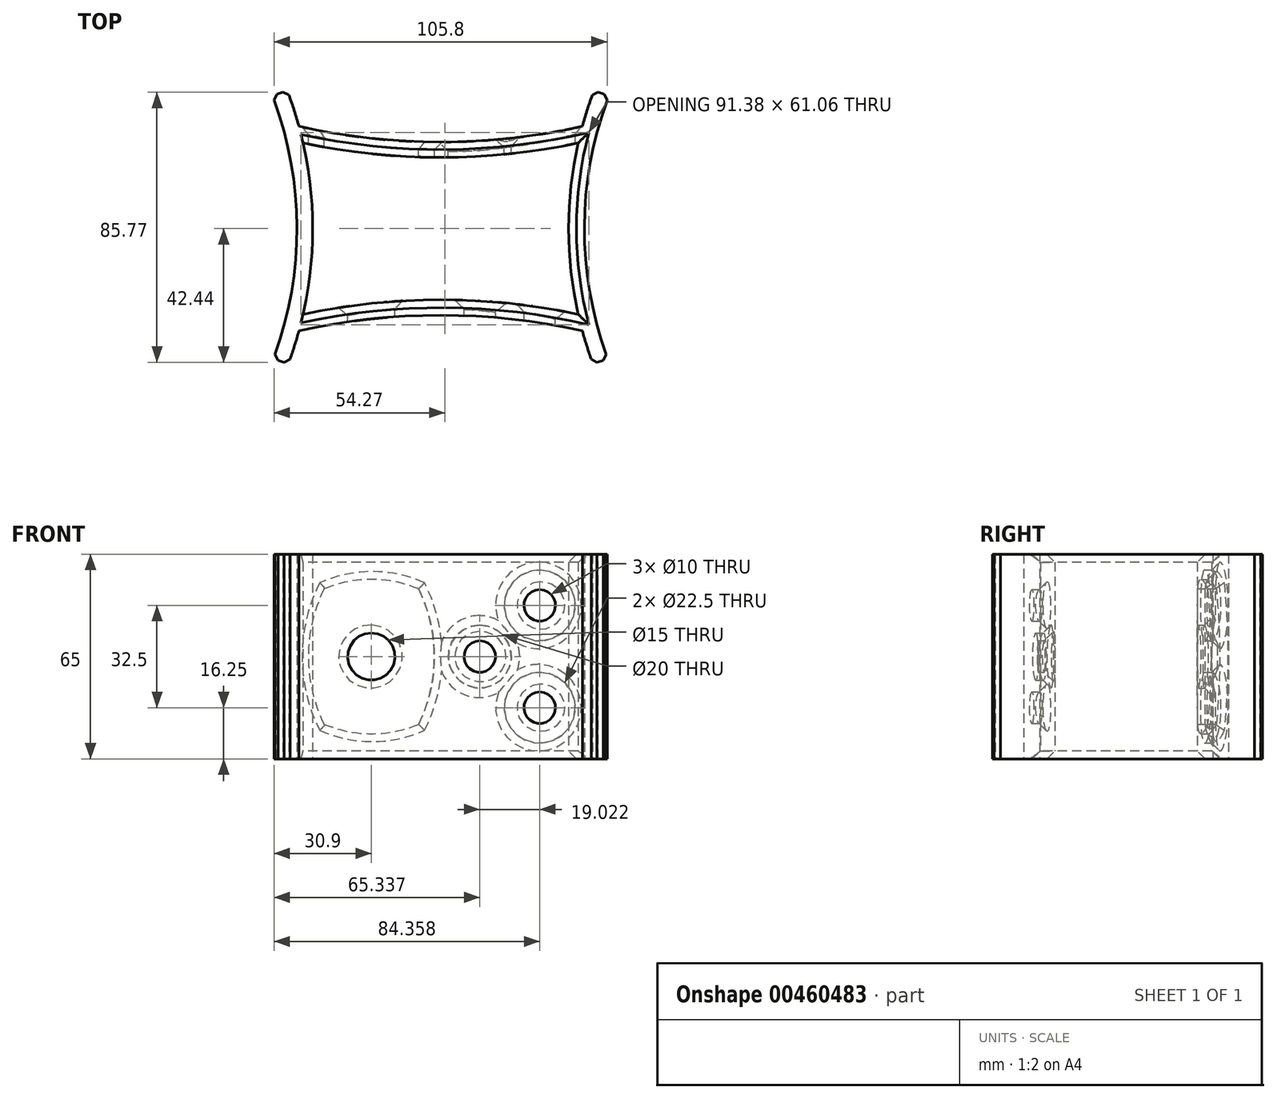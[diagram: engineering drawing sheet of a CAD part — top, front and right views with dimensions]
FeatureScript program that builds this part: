
annotation { "Feature Type Name" : "Feature", "Feature Type Description" : "" }
export const myFeature = defineFeature(function(context is Context, id is Id, definition is map)
    precondition{}
    {
        {
            var Q0;
            Q0=qCreatedBy(makeId("Top.planeOp"),FACE);
            var sketch = newSketch(context, id + "F0", { "sketchPlane" : qUnion([Q0])});
            skLineSegment(sketch, "E0.bottom", {"start": v(0, 0) * mm, "end": v(90, 0) * mm, "construction": true});
            skLineSegment(sketch, "E0.top", {"start": v(0, -5) * mm, "end": v(90, -5) * mm, "construction": true});
            skLineSegment(sketch, "E0.left", {"start": v(0, 0) * mm, "end": v(0, -5) * mm});
            skLineSegment(sketch, "E0.right", {"start": v(90, 0) * mm, "end": v(90, -5) * mm});
            skArc(sketch, "E1", {"start": v(0, 0) * mm, "mid": v(45, -5) * mm, "end": v(90, 0) * mm});
            skArc(sketch, "E2", {"start": v(0, -5) * mm, "mid": v(45, -9.88) * mm, "end": v(90, -5) * mm});
            skLineSegment(sketch, "E3", {"start": v(0, 0) * mm, "end": v(0, -65) * mm, "construction": true});
            skLineSegment(sketch, "E4", {"start": v(0, -32.5) * mm, "end": v(-19.4, -32.5) * mm});
            skLineSegment(sketch, "E5.MirrorCS", {"start": v(90, -65) * mm, "end": v(90, -60) * mm});
            skLineSegment(sketch, "E6.MirrorCS", {"start": v(0, -65) * mm, "end": v(0, -60) * mm});
            skArc(sketch, "E7.MirrorCS", {"start": v(0, -60) * mm, "mid": v(45, -55.12) * mm, "end": v(90, -60) * mm});
            skArc(sketch, "E8.MirrorCS", {"start": v(0, -65) * mm, "mid": v(45, -60) * mm, "end": v(90, -65) * mm});
            skArc(sketch, "E9", {"start": v(98.46, 9.78) * mm, "mid": v(90.63, -32.05) * mm, "end": v(98.14, -73.94) * mm});
            skLineSegment(sketch, "E10", {"start": v(90, 0) * mm, "end": v(90, -65) * mm, "construction": true});
            skLineSegment(sketch, "E11", {"start": v(90, -32.5) * mm, "end": v(208.75, -32.5) * mm, "construction": true});
            skArc(sketch, "E12.0", {"start": v(93.66, 11.24) * mm, "mid": v(85.63, -32.01) * mm, "end": v(93.32, -75.33) * mm});
            skLineSegment(sketch, "E13", {"start": v(93.32, -75.33) * mm, "end": v(98.14, -73.94) * mm});
            skLineSegment(sketch, "E14", {"start": v(98.46, 9.78) * mm, "end": v(93.66, 11.24) * mm});
            skLineSegment(sketch, "E15", {"start": v(45, 0) * mm, "end": v(45, 27.4) * mm});
            skArc(sketch, "E16.MirrorCS", {"start": v(-8.46, 9.78) * mm, "mid": v(-0.63, -32.05) * mm, "end": v(-8.14, -73.94) * mm});
            skArc(sketch, "E17.MirrorCS", {"start": v(-3.66, 11.24) * mm, "mid": v(4.37, -32.01) * mm, "end": v(-3.32, -75.33) * mm});
            skLineSegment(sketch, "E18.MirrorCS", {"start": v(-8.46, 9.78) * mm, "end": v(-3.66, 11.24) * mm});
            skLineSegment(sketch, "E19.MirrorCS", {"start": v(-3.32, -75.33) * mm, "end": v(-8.14, -73.94) * mm});
            skSolve(sketch);
        }
        {
            var Q0;
            Q0=qSketchRegion(id+"F0",true);
            extrude(context, id + "F1", {"entities" : qUnion([Q0]), "depth" : 65 * mm});
        }
        {
            var Q0;
            Q0=qCreatedBy(makeId("Front.planeOp"),FACE);
            var sketch = newSketch(context, id + "F2", { "sketchPlane" : qUnion([Q0])});
            skLineSegment(sketch, "E20.0.0", {"start": v(90, 0) * mm, "end": v(0, 0) * mm, "construction": true});
            skLineSegment(sketch, "E20.0.1", {"start": v(0, 0) * mm, "end": v(0, 65) * mm, "construction": true});
            skLineSegment(sketch, "E20.0.2", {"start": v(0, 65) * mm, "end": v(90, 65) * mm, "construction": true});
            skLineSegment(sketch, "E20.0.3", {"start": v(90, 65) * mm, "end": v(90, 0) * mm, "construction": true});
            skLineSegment(sketch, "E21", {"start": v(45, 0) * mm, "end": v(45, 65) * mm, "construction": true});
            skLineSegment(sketch, "E22", {"start": v(45, 65) * mm, "end": v(45.5, 64.29) * mm, "construction": true});
            skLineSegment(sketch, "E23", {"start": v(46, 65) * mm, "end": v(0, 0) * mm, "construction": true});
            skLineSegment(sketch, "E24.bottom", {"start": v(38, 11) * mm, "end": v(8, 11) * mm, "construction": true});
            skLineSegment(sketch, "E24.top", {"start": v(38, 54) * mm, "end": v(8, 54) * mm, "construction": true});
            skLineSegment(sketch, "E24.left", {"start": v(38, 11) * mm, "end": v(38, 54) * mm, "construction": true});
            skLineSegment(sketch, "E24.right", {"start": v(8, 11) * mm, "end": v(8, 54) * mm, "construction": true});
            skPoint(sketch, "E24.middle", {"position": v(23, 32.5) * mm});
            skArc(sketch, "E25", {"start": v(38, 11) * mm, "mid": v(43, 32.5) * mm, "end": v(38, 54) * mm});
            skLineSegment(sketch, "E26", {"start": v(23, 11) * mm, "end": v(23, 54) * mm, "construction": true});
            skArc(sketch, "E27.MirrorCS", {"start": v(8, 11) * mm, "mid": v(3, 32.5) * mm, "end": v(8, 54) * mm});
            skArc(sketch, "E28", {"start": v(8, 11) * mm, "mid": v(23, 8) * mm, "end": v(38, 11) * mm});
            skArc(sketch, "E29", {"start": v(38, 54) * mm, "mid": v(23, 57) * mm, "end": v(8, 54) * mm});
            skLineSegment(sketch, "E30", {"start": v(67.5, 32.5) * mm, "end": v(67.5, 0) * mm, "construction": true});
            skCircle(sketch, "E31", {"center": v(76.46, 16.25) * mm, "radius": 11.25 * mm});
            skCircle(sketch, "E32.MirrorC", {"center": v(76.46, 48.75) * mm, "radius": 11.25 * mm});
            skPoint(sketch, "E33.end.orphan", {"position": v(90, 32.5) * mm});
            skSolve(sketch);
        }
        {
            var Q0;
            Q0=qSketchRegion(id+"F2",true);
            extrude(context, id + "F3", {"entities" : qUnion([Q0]), "operationType" : NewBodyOperationType.REMOVE, "depth" : 10 * mm});
        }
        {
            var Q0;
            Q0=qCreatedBy(makeId("Front.planeOp"),FACE);
            var sketch = newSketch(context, id + "F4", { "sketchPlane" : qUnion([Q0])});
            skLineSegment(sketch, "E34.0", {"start": v(46, 65) * mm, "end": v(0, 0) * mm, "construction": true});
            skCircle(sketch, "E35", {"center": v(23, 32.5) * mm, "radius": 7.5 * mm});
            skCircle(sketch, "E36", {"center": v(76.46, 16.25) * mm, "radius": 5 * mm});
            skCircle(sketch, "E37.MirrorC", {"center": v(76.46, 48.75) * mm, "radius": 5 * mm});
            skPoint(sketch, "E34.2.end.orphan", {"position": v(90, 32.5) * mm});
            skPoint(sketch, "E34.2.start.orphan", {"position": v(67.5, 32.5) * mm});
            skPoint(sketch, "E38.orphan", {"position": v(67.5, 0) * mm});
            skPoint(sketch, "E34.1.start.orphan", {"position": v(67.5, 32.5) * mm});
            skSolve(sketch);
        }
        {
            var Q0;
            Q0=qSketchRegion(id+"F4",true);
            extrude(context, id + "F5", {"entities" : qUnion([Q0]), "operationType" : NewBodyOperationType.REMOVE, "depth" : 80 * mm});
        }
        {
            var Q0;
            Q0=makeQuery(id+"F1.opExtrude","SWEPT_EDGE",EDGE,{"disambiguationData":[OSD([sQuery(id+"F0.wireOp",EDGE,"E16.MirrorCS"),sQuery(id+"F0.wireOp",EDGE,"E18.MirrorCS")])]});
            var Q1;
            Q1=makeQuery(id+"F1.opExtrude","SWEPT_EDGE",EDGE,{"disambiguationData":[OSD([sQuery(id+"F0.wireOp",EDGE,"E17.MirrorCS"),sQuery(id+"F0.wireOp",EDGE,"E18.MirrorCS")])]});
            var Q2;
            Q2=makeQuery(id+"F1.opExtrude","SWEPT_EDGE",EDGE,{"disambiguationData":[OSD([sQuery(id+"F0.wireOp",EDGE,"E12.0"),sQuery(id+"F0.wireOp",EDGE,"E14")])]});
            var Q3;
            Q3=makeQuery(id+"F1.opExtrude","SWEPT_EDGE",EDGE,{"disambiguationData":[OSD([sQuery(id+"F0.wireOp",EDGE,"E9"),sQuery(id+"F0.wireOp",EDGE,"E14")])]});
            var Q4;
            Q4=makeQuery(id+"F1.opExtrude","SWEPT_EDGE",EDGE,{"disambiguationData":[OSD([sQuery(id+"F0.wireOp",EDGE,"E17.MirrorCS"),sQuery(id+"F0.wireOp",EDGE,"E19.MirrorCS")])]});
            var Q5;
            Q5=makeQuery(id+"F1.opExtrude","SWEPT_EDGE",EDGE,{"disambiguationData":[OSD([sQuery(id+"F0.wireOp",EDGE,"E16.MirrorCS"),sQuery(id+"F0.wireOp",EDGE,"E19.MirrorCS")])]});
            var Q6;
            Q6=makeQuery(id+"F1.opExtrude","SWEPT_EDGE",EDGE,{"disambiguationData":[OSD([sQuery(id+"F0.wireOp",EDGE,"E12.0"),sQuery(id+"F0.wireOp",EDGE,"E13")])]});
            var Q7;
            Q7=makeQuery(id+"F1.opExtrude","SWEPT_EDGE",EDGE,{"disambiguationData":[OSD([sQuery(id+"F0.wireOp",EDGE,"E9"),sQuery(id+"F0.wireOp",EDGE,"E13")])]});
            chamfer(context, id + "F6", {"entities" : qUnion([Q0, Q1, Q2, Q3, Q4, Q5, Q6, Q7]), "width" : 1.5 * mm, "tangentPropagation" : true});
        }
        {
            var Q0;
            Q0=makeQuery(id+"F1.opExtrude","CAP_EDGE",EDGE,{"disambiguationData":[OSD([sQuery(id+"F0.wireOp",EDGE,"E2")])],"isStart":false});
            var Q1;
            {var subQ0=sQuery(id+"F0.wireOp",EDGE,"E17.MirrorCS");Q1=makeQuery(id+"F1.opExtrude","CAP_EDGE",EDGE,{"disambiguationData":[OSD([subQ0]),TDD([makeQuery(id+"F0.imprint","IMPRINT",EDGE,{"disambiguationData":[TD([[makeQuery(id+"F0.imprint","INTERSECT",VERTEX,{"derivedFrom":[sQuery(id+"F0.wireOp",EDGE,"E2"),subQ0]}),-1.0]])],"derivedFrom":subQ0})])],"isStart":false});}
            var Q2;
            Q2=makeQuery(id+"F1.opExtrude","CAP_EDGE",EDGE,{"disambiguationData":[OSD([sQuery(id+"F0.wireOp",EDGE,"E7.MirrorCS")])],"isStart":false});
            var Q3;
            {var subQ0=sQuery(id+"F0.wireOp",EDGE,"E12.0");Q3=makeQuery(id+"F1.opExtrude","CAP_EDGE",EDGE,{"disambiguationData":[OSD([subQ0]),TDD([makeQuery(id+"F0.imprint","IMPRINT",EDGE,{"disambiguationData":[TD([[makeQuery(id+"F0.imprint","INTERSECT",VERTEX,{"derivedFrom":[sQuery(id+"F0.wireOp",EDGE,"E2"),subQ0]}),-1.0]])],"derivedFrom":subQ0})])],"isStart":false});}
            var Q4;
            Q4=makeQuery(id+"F1.opExtrude","CAP_EDGE",EDGE,{"disambiguationData":[OSD([sQuery(id+"F0.wireOp",EDGE,"E2")])],"isStart":true});
            var Q5;
            {var subQ0=sQuery(id+"F0.wireOp",EDGE,"E12.0");Q5=makeQuery(id+"F1.opExtrude","CAP_EDGE",EDGE,{"disambiguationData":[OSD([subQ0]),TDD([makeQuery(id+"F0.imprint","IMPRINT",EDGE,{"disambiguationData":[TD([[makeQuery(id+"F0.imprint","INTERSECT",VERTEX,{"derivedFrom":[sQuery(id+"F0.wireOp",EDGE,"E2"),subQ0]}),-1.0]])],"derivedFrom":subQ0})])],"isStart":true});}
            var Q6;
            Q6=makeQuery(id+"F1.opExtrude","CAP_EDGE",EDGE,{"disambiguationData":[OSD([sQuery(id+"F0.wireOp",EDGE,"E7.MirrorCS")])],"isStart":true});
            var Q7;
            {var subQ0=sQuery(id+"F0.wireOp",EDGE,"E17.MirrorCS");Q7=makeQuery(id+"F1.opExtrude","CAP_EDGE",EDGE,{"disambiguationData":[OSD([subQ0]),TDD([makeQuery(id+"F0.imprint","IMPRINT",EDGE,{"disambiguationData":[TD([[makeQuery(id+"F0.imprint","INTERSECT",VERTEX,{"derivedFrom":[sQuery(id+"F0.wireOp",EDGE,"E2"),subQ0]}),-1.0]])],"derivedFrom":subQ0})])],"isStart":true});}
            chamfer(context, id + "F7", {"entities" : qUnion([Q0, Q1, Q2, Q3, Q4, Q5, Q6, Q7]), "width" : 2.5 * mm, "tangentPropagation" : true});
        }
        {
            var Q0;
            Q0=makeQuery(id+"F3.boolean.opBoolean","INTERSECT",EDGE,{"derivedFrom":[makeQuery(id+"F1.opExtrude","SWEPT_FACE",FACE,{"disambiguationData":[OSD([sQuery(id+"F0.wireOp",EDGE,"E1")])]}),makeQuery(id+"F3.opExtrude","SWEPT_FACE",FACE,{"disambiguationData":[OSD([sQuery(id+"F2.wireOp",EDGE,"E28")])]})]});
            var Q1;
            Q1=makeQuery(id+"F3.boolean.opBoolean","INTERSECT",EDGE,{"derivedFrom":[makeQuery(id+"F1.opExtrude","SWEPT_FACE",FACE,{"disambiguationData":[OSD([sQuery(id+"F0.wireOp",EDGE,"E1")])]}),makeQuery(id+"F3.opExtrude","SWEPT_FACE",FACE,{"disambiguationData":[OSD([sQuery(id+"F2.wireOp",EDGE,"E25")])]})]});
            var Q2;
            Q2=makeQuery(id+"F3.boolean.opBoolean","INTERSECT",EDGE,{"derivedFrom":[makeQuery(id+"F1.opExtrude","SWEPT_FACE",FACE,{"disambiguationData":[OSD([sQuery(id+"F0.wireOp",EDGE,"E1")])]}),makeQuery(id+"F3.opExtrude","SWEPT_FACE",FACE,{"disambiguationData":[OSD([sQuery(id+"F2.wireOp",EDGE,"E27.MirrorCS")])]})]});
            var Q3;
            Q3=makeQuery(id+"F3.boolean.opBoolean","INTERSECT",EDGE,{"derivedFrom":[makeQuery(id+"F1.opExtrude","SWEPT_FACE",FACE,{"disambiguationData":[OSD([sQuery(id+"F0.wireOp",EDGE,"E1")])]}),makeQuery(id+"F3.opExtrude","SWEPT_FACE",FACE,{"disambiguationData":[OSD([sQuery(id+"F2.wireOp",EDGE,"E29")])]})]});
            var Q4;
            Q4=makeQuery(id+"F3.boolean.opBoolean","INTERSECT",EDGE,{"derivedFrom":[makeQuery(id+"F1.opExtrude","SWEPT_FACE",FACE,{"disambiguationData":[OSD([sQuery(id+"F0.wireOp",EDGE,"E1")])]}),makeQuery(id+"F3.opExtrude","SWEPT_FACE",FACE,{"disambiguationData":[OSD([sQuery(id+"F2.wireOp",EDGE,"E31")])]})]});
            var Q5;
            Q5=makeQuery(id+"F3.boolean.opBoolean","INTERSECT",EDGE,{"derivedFrom":[makeQuery(id+"F1.opExtrude","SWEPT_FACE",FACE,{"disambiguationData":[OSD([sQuery(id+"F0.wireOp",EDGE,"E1")])]}),makeQuery(id+"F3.opExtrude","SWEPT_FACE",FACE,{"disambiguationData":[OSD([sQuery(id+"F2.wireOp",EDGE,"E32.MirrorC")])]})]});
            var Q6;
            Q6=makeQuery(id+"F5.boolean.opBoolean","INTERSECT",EDGE,{"derivedFrom":[makeQuery(id+"F1.opExtrude","SWEPT_FACE",FACE,{"disambiguationData":[OSD([sQuery(id+"F0.wireOp",EDGE,"E7.MirrorCS")])]}),makeQuery(id+"F5.opExtrude","SWEPT_FACE",FACE,{"disambiguationData":[OSD([sQuery(id+"F4.wireOp",EDGE,"E35")])]})]});
            var Q7;
            Q7=makeQuery(id+"F5.boolean.opBoolean","INTERSECT",EDGE,{"derivedFrom":[makeQuery(id+"F1.opExtrude","SWEPT_FACE",FACE,{"disambiguationData":[OSD([sQuery(id+"F0.wireOp",EDGE,"E7.MirrorCS")])]}),makeQuery(id+"F5.opExtrude","SWEPT_FACE",FACE,{"disambiguationData":[OSD([sQuery(id+"F4.wireOp",EDGE,"E36")])]})]});
            var Q8;
            Q8=makeQuery(id+"F5.boolean.opBoolean","INTERSECT",EDGE,{"derivedFrom":[makeQuery(id+"F1.opExtrude","SWEPT_FACE",FACE,{"disambiguationData":[OSD([sQuery(id+"F0.wireOp",EDGE,"E7.MirrorCS")])]}),makeQuery(id+"F5.opExtrude","SWEPT_FACE",FACE,{"disambiguationData":[OSD([sQuery(id+"F4.wireOp",EDGE,"E37.MirrorC")])]})]});
            chamfer(context, id + "F8", {"entities" : qUnion([Q0, Q1, Q2, Q3, Q4, Q5, Q6, Q7, Q8]), "width" : 2.5 * mm, "tangentPropagation" : true});
        }
        {
            var Q0;
            Q0=qCreatedBy(makeId("Front.planeOp"),FACE);
            var sketch = newSketch(context, id + "F9", { "sketchPlane" : qUnion([Q0])});
            skLineSegment(sketch, "E39", {"start": v(67.65, 32.5) * mm, "end": v(50.06, 32.5) * mm, "construction": true});
            skCircle(sketch, "E40", {"center": v(57.44, 32.5) * mm, "radius": 10 * mm});
            skSolve(sketch);
        }
        {
            var Q0;
            Q0 = qSketchRegion(id + "F9", true);
            extrude(context, id + "F10", {"entities" : qUnion([Q0]), "operationType" : NewBodyOperationType.REMOVE, "depth" : 25 * mm});
        }
        {
            var Q0;
            Q0=makeQuery(id+"F10.boolean.opBoolean","INTERSECT",EDGE,{"derivedFrom":[makeQuery(id+"F1.opExtrude","SWEPT_FACE",FACE,{"disambiguationData":[OSD([sQuery(id+"F0.wireOp",EDGE,"E1")])]}),makeQuery(id+"F10.opExtrude","SWEPT_FACE",FACE,{"disambiguationData":[OSD([sQuery(id+"F9.wireOp",EDGE,"E40")])]})]});
            chamfer(context, id + "F11", {"entities" : qUnion([Q0]), "width" : 3 * mm, "tangentPropagation" : true});
        }
        {
            var Q0;
            Q0=qCreatedBy(makeId("Front.planeOp"),FACE);
            var sketch = newSketch(context, id + "F12", { "sketchPlane" : qUnion([Q0])});
            skCircle(sketch, "E41", {"center": v(57.44, 32.5) * mm, "radius": 5 * mm});
            skSolve(sketch);
        }
        {
            var Q0;
            Q0 = qSketchRegion(id + "F12", true);
            extrude(context, id + "F13", {"entities" : qUnion([Q0]), "operationType" : NewBodyOperationType.REMOVE, "depth" : 70 * mm});
        }
        {
            var Q0;
            Q0=makeQuery(id+"F13.boolean.opBoolean","INTERSECT",EDGE,{"derivedFrom":[makeQuery(id+"F1.opExtrude","SWEPT_FACE",FACE,{"disambiguationData":[OSD([sQuery(id+"F0.wireOp",EDGE,"E7.MirrorCS")])]}),makeQuery(id+"F13.opExtrude","SWEPT_FACE",FACE,{"disambiguationData":[OSD([sQuery(id+"F12.wireOp",EDGE,"E41")])]})]});
            chamfer(context, id + "F14", {"entities" : qUnion([Q0]), "width" : 3 * mm});
        }
    });
